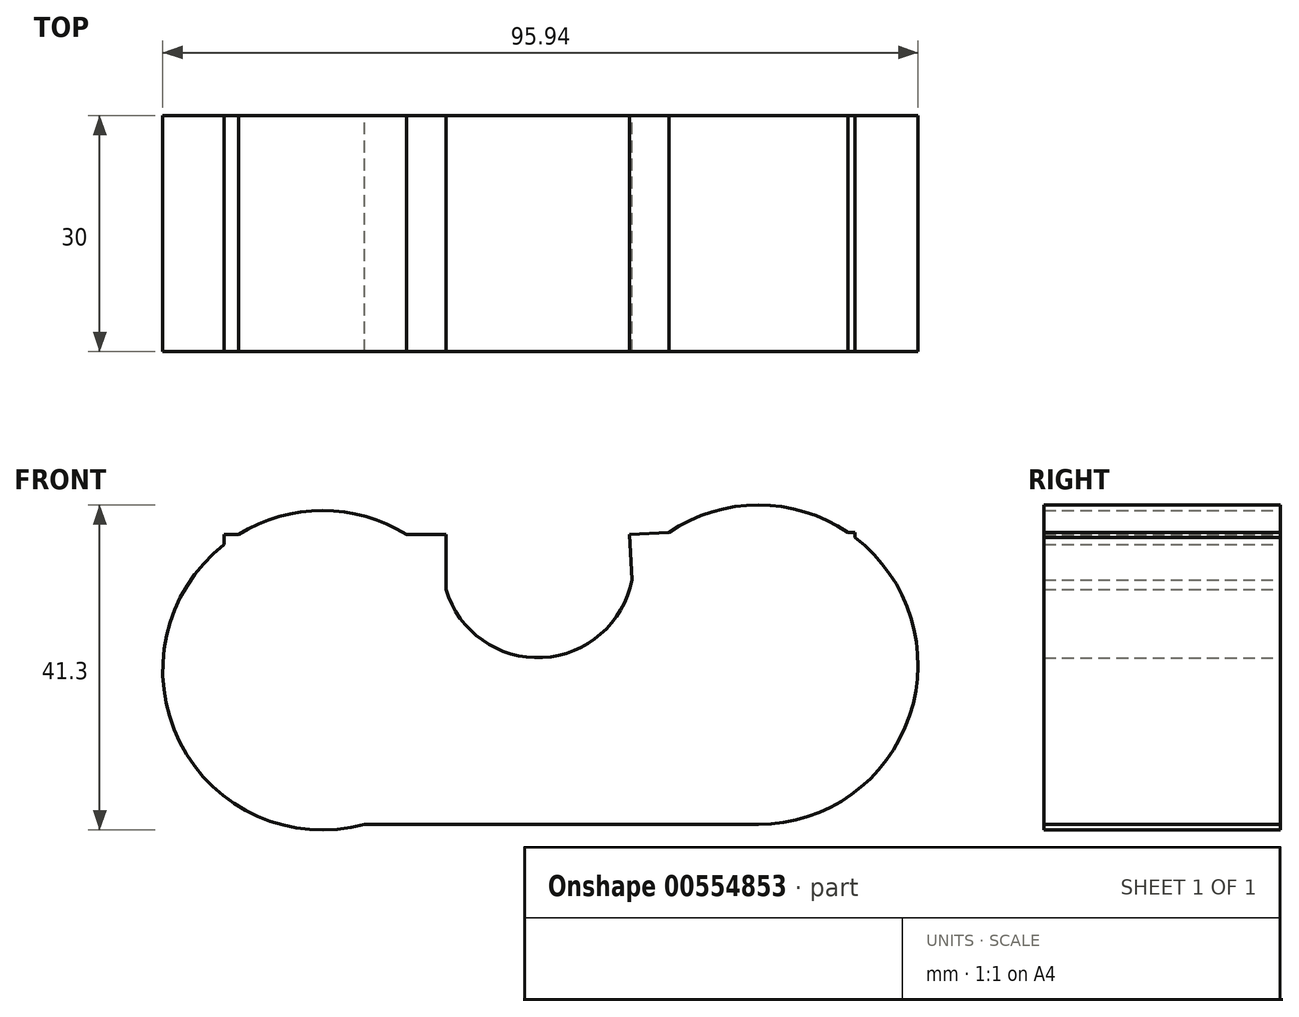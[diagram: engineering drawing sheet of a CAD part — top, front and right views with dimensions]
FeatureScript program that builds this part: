
annotation { "Feature Type Name" : "Feature", "Feature Type Description" : "" }
export const myFeature = defineFeature(function(context is Context, id is Id, definition is map)
    precondition{}
    {
        {
            var Q0;
            Q0=qCreatedBy(makeId("Front.planeOp"),FACE);
            var sketch = newSketch(context, id + "F0", { "sketchPlane" : qUnion([Q0])});
            skLineSegment(sketch, "E0", {"start": v(-17.8, -46.34) * mm, "end": v(32.2, -46.34) * mm});
            skLineSegment(sketch, "E1", {"start": v(-7.48, -9.5) * mm, "end": v(-7.48, -16.48) * mm});
            skLineSegment(sketch, "E2", {"start": v(16.13, -15.27) * mm, "end": v(15.83, -9.5) * mm});
            skArc(sketch, "E3", {"start": v(-7.48, -16.48) * mm, "mid": v(4.8, -25.14) * mm, "end": v(16.13, -15.27) * mm});
            skLineSegment(sketch, "E4", {"start": v(15.83, -9.5) * mm, "end": v(20.82, -9.24) * mm});
            skLineSegment(sketch, "E5", {"start": v(-7.48, -9.5) * mm, "end": v(-12.48, -9.5) * mm});
            skLineSegment(sketch, "E6", {"start": v(-33.83, -9.5) * mm, "end": v(-35.7, -9.5) * mm});
            skLineSegment(sketch, "E7", {"start": v(-35.7, -9.5) * mm, "end": v(-35.7, -10.8) * mm});
            skLineSegment(sketch, "E8", {"start": v(43.57, -9.24) * mm, "end": v(44.47, -9.24) * mm});
            skLineSegment(sketch, "E9", {"start": v(44.47, -9.24) * mm, "end": v(44.47, -9.9) * mm});
            skArc(sketch, "E10", {"start": v(-12.48, -9.5) * mm, "mid": v(-43.24, -23.86) * mm, "end": v(-17.8, -46.34) * mm});
            skArc(sketch, "E11", {"start": v(32.2, -46.34) * mm, "mid": v(51.6, -20.1) * mm, "end": v(20.82, -9.24) * mm});
            skPoint(sketch, "E12.trimOffspring.end.orphan", {"position": v(44.47, -46.34) * mm});
            skSolve(sketch);
        }
        {
            var Q0;
            Q0 = qSketchRegion(id + "F0", true);
            extrude(context, id + "F1", {"entities" : qUnion([Q0]), "depth" : 30 * mm, "offsetDistance" : 25 * mm});
        }
    });
